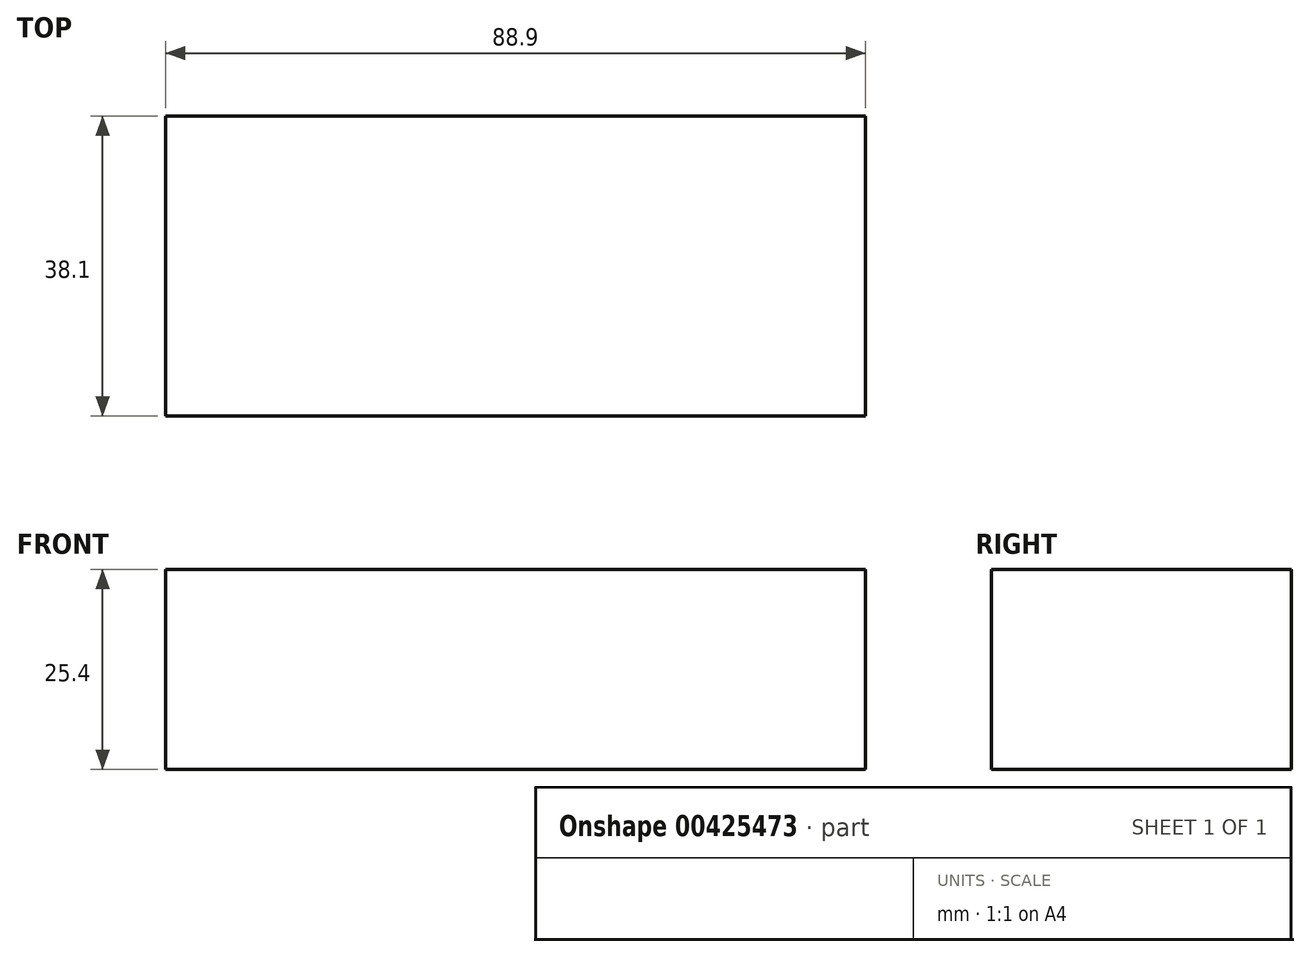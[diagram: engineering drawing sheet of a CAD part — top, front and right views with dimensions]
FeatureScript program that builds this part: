
annotation { "Feature Type Name" : "Feature", "Feature Type Description" : "" }
export const myFeature = defineFeature(function(context is Context, id is Id, definition is map)
    precondition{}
    {
        {
            var Q0;
            Q0=qCreatedBy(makeId("Top.planeOp"),FACE);
            var sketch = newSketch(context, id + "F0", { "sketchPlane" : qUnion([Q0])});
            skLineSegment(sketch, "E0.bottom", {"start": v(44.45, 19.05) * mm, "end": v(-44.45, 19.05) * mm});
            skLineSegment(sketch, "E0.top", {"start": v(44.45, -19.05) * mm, "end": v(-44.45, -19.05) * mm});
            skLineSegment(sketch, "E0.left", {"start": v(44.45, 19.05) * mm, "end": v(44.45, -19.05) * mm});
            skLineSegment(sketch, "E0.right", {"start": v(-44.45, 19.05) * mm, "end": v(-44.45, -19.05) * mm});
            skPoint(sketch, "E0.middle", {"position": v(0, 0) * mm});
            skSolve(sketch);
        }
        {
            var Q0;
            Q0=makeQuery(id+"F0.imprint","IMPRINT",FACE,{"disambiguationData":[TD([[makeQuery(id+"F0.imprint","IMPRINT",EDGE,{"derivedFrom":sQuery(id+"F0.wireOp",EDGE,"E0.bottom")}),1.0]])]});
            extrude(context, id + "F1", {"entities" : qUnion([Q0]), "depth" : 25.4 * mm});
        }
    });
